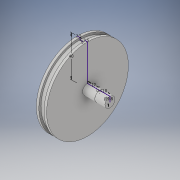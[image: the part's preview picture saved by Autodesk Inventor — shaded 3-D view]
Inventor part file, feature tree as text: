
AUTODESK INVENTOR PART (.ipt)
format: ipt  version: 2019 (Build 230136000, 136)  size: 125,952 bytes
history: native  units: in
note: dims shown in document units (in); Inventor stores cm internally (conversion verified against a paired STEP export)
features: revolve x1, sketch x1
ambient origin geometry x8: Origin, YZ Plane, XZ Plane, XY Plane, X Axis, Y Axis, Z Axis, Center Point
bodies: Solid1 (feature_tree)
feature tree (2):
  revolve  "Revolution1"  [1 undecoded]
  sketch  "Sketch1"  dims[d0=1.5748in d1=0.0984in d2=0.0787in d3=0.1969in d4=0.0984in d6=0.4724in d7=0.0039in d8=0.3937in d9=90.0deg d11=0.3858in]
note: 1 required parameter value undecoded (feature->parameter linkage not recoverable at this tier; creation-order binding heuristic only, values carry confidence <= 0.55)
